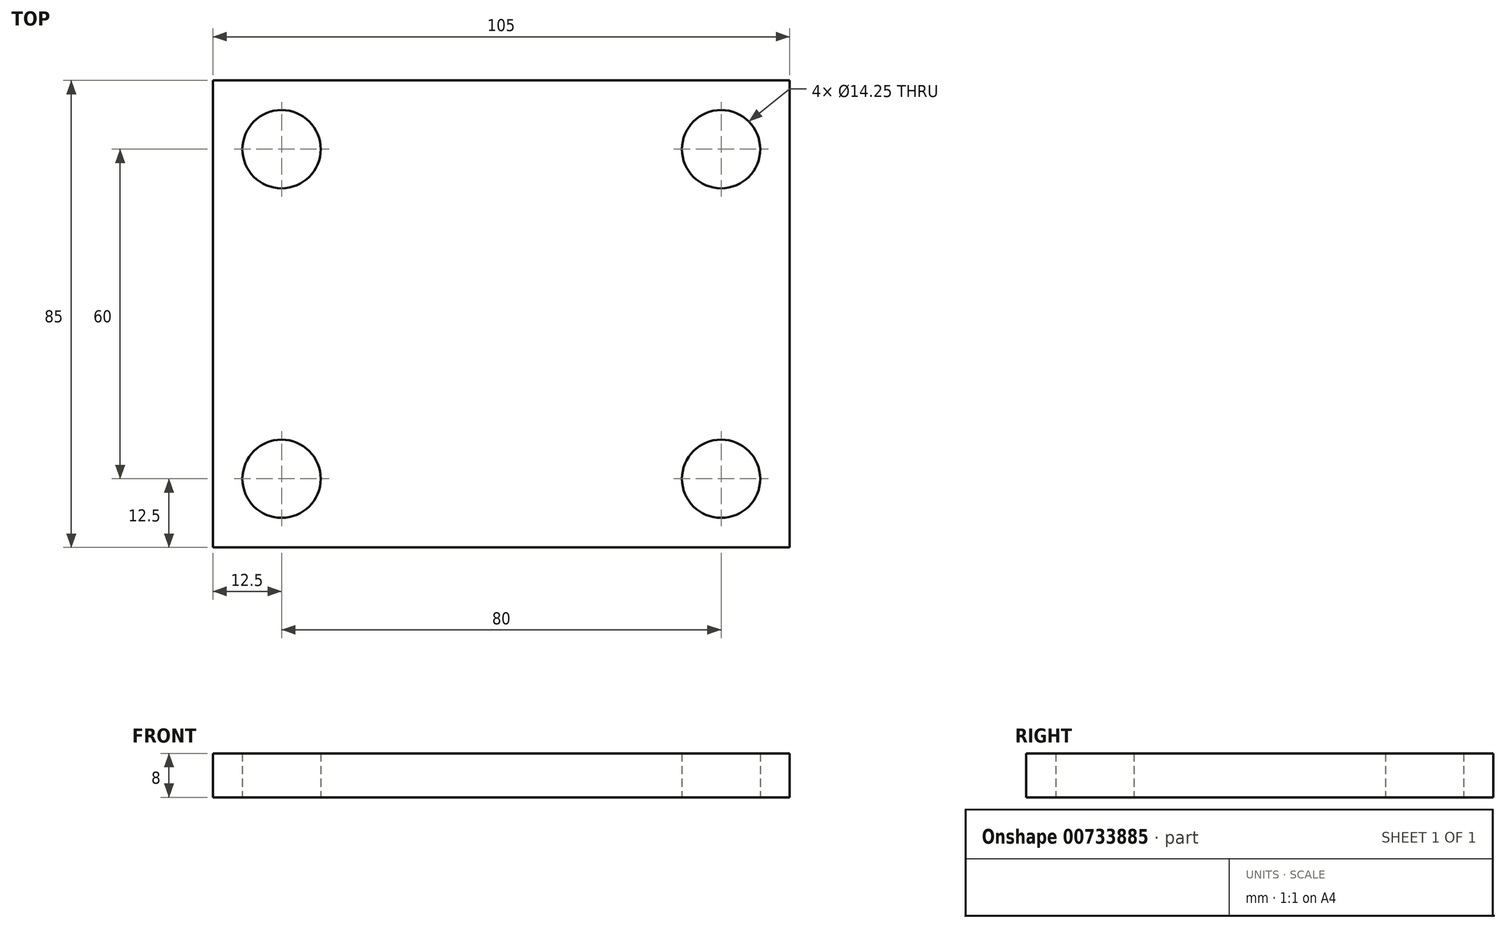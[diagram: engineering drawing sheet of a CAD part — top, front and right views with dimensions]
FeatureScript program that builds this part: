
annotation { "Feature Type Name" : "Feature", "Feature Type Description" : "" }
export const myFeature = defineFeature(function(context is Context, id is Id, definition is map)
    precondition{}
    {
        {
            var Q0;
            Q0=qCreatedBy(makeId("Top.planeOp"),FACE);
            var sketch = newSketch(context, id + "F0", { "sketchPlane" : qUnion([Q0])});
            skLineSegment(sketch, "E0.bottom", {"start": v(52.5, 42.5) * mm, "end": v(-52.5, 42.5) * mm});
            skLineSegment(sketch, "E0.top", {"start": v(52.5, -42.5) * mm, "end": v(-52.5, -42.5) * mm});
            skLineSegment(sketch, "E0.left", {"start": v(52.5, 42.5) * mm, "end": v(52.5, -42.5) * mm});
            skLineSegment(sketch, "E0.right", {"start": v(-52.5, 42.5) * mm, "end": v(-52.5, -42.5) * mm});
            skPoint(sketch, "E0.middle", {"position": v(0, 0) * mm});
            skCircle(sketch, "E1", {"center": v(-40, 30) * mm, "radius": 4 * mm});
            skCircle(sketch, "E2", {"center": v(40, 30) * mm, "radius": 4 * mm});
            skCircle(sketch, "E3", {"center": v(-40, -30) * mm, "radius": 4 * mm});
            skCircle(sketch, "E4", {"center": v(40, -30) * mm, "radius": 4 * mm});
            skSolve(sketch);
        }
        {
            var Q0;
            Q0=makeQuery(id+"F0.imprint","IMPRINT",FACE,{"disambiguationData":[TD([[makeQuery(id+"F0.imprint","IMPRINT",EDGE,{"derivedFrom":sQuery(id+"F0.wireOp",EDGE,"E0.bottom")}),1.0]])]});
            var Q1;
            Q1=makeQuery(id+"F0.imprint","IMPRINT",FACE,{"disambiguationData":[TD([[makeQuery(id+"F0.imprint","IMPRINT",EDGE,{"derivedFrom":sQuery(id+"F0.wireOp",EDGE,"E1")}),1.0]])]});
            var Q2;
            Q2=makeQuery(id+"F0.imprint","IMPRINT",FACE,{"disambiguationData":[TD([[makeQuery(id+"F0.imprint","IMPRINT",EDGE,{"derivedFrom":sQuery(id+"F0.wireOp",EDGE,"E2")}),1.0]])]});
            var Q3;
            Q3=makeQuery(id+"F0.imprint","IMPRINT",FACE,{"disambiguationData":[TD([[makeQuery(id+"F0.imprint","IMPRINT",EDGE,{"derivedFrom":sQuery(id+"F0.wireOp",EDGE,"E4")}),1.0]])]});
            var Q4;
            Q4=makeQuery(id+"F0.imprint","IMPRINT",FACE,{"disambiguationData":[TD([[makeQuery(id+"F0.imprint","IMPRINT",EDGE,{"derivedFrom":sQuery(id+"F0.wireOp",EDGE,"E3")}),1.0]])]});
            extrude(context, id + "F1", {"entities" : qUnion([Q0, Q1, Q2, Q3, Q4]), "depth" : 8 * mm, "offsetDistance" : 25 * mm});
        }
        {
            var Q0;
            Q0=sQuery(id+"F0.wireOp",VERTEX,"E1.center");
            var Q1;
            Q1=sQuery(id+"F0.wireOp",VERTEX,"E2.center");
            var Q2;
            Q2=sQuery(id+"F0.wireOp",VERTEX,"E4.center");
            var Q3;
            Q3=sQuery(id+"F0.wireOp",VERTEX,"E3.center");
            var Q4;
            Q4=makeQuery(id+"F1.opExtrude","SWEPT_BODY",BODY,{"disambiguationData":[OSD([sQuery(id+"F0.wireOp",EDGE,"E0.bottom"),sQuery(id+"F0.wireOp",EDGE,"E0.top"),sQuery(id+"F0.wireOp",EDGE,"E0.left"),sQuery(id+"F0.wireOp",EDGE,"E0.right")])]});
            hole(context, id + "F2", {"style" : HoleStyle.C_BORE, "endStyle" : HoleEndStyle.THROUGH, "oppositeDirection" : true, "standardTappedOrClearance" : lookupTablePath({ "standard" : "ISO", "fit" : "Normal", "size" : "M8", "type" : "Clearance" }), "standardBlindInLast" : lookupTablePath({ "fit" : "Standard", "standard" : "ISO", "size" : "M8", "type" : "Clearance" }), "holeDiameter" : 8.8 * mm, "cBoreDiameter" : 14.25 * mm, "cBoreDepth" : 8 * mm, "majorDiameter" : 5 * mm, "isTappedThrough" : true, "tappedDepth" : 12 * mm, "tapClearance" : 3, "locations" : qUnion([Q0, Q1, Q2, Q3]), "scope" : qUnion([Q4])});
        }
    });
